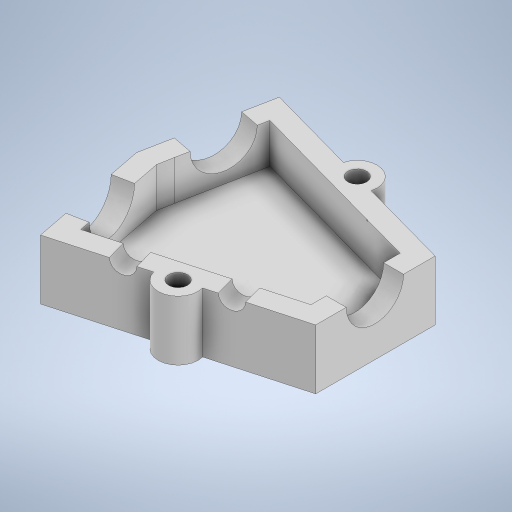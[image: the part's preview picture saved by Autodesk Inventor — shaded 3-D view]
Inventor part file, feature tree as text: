
AUTODESK INVENTOR PART (.ipt)
format: ipt  version: 2024 (Build 280153000, 153)  size: 346,624 bytes
history: native  units: in
note: dims shown in document units (in); Inventor stores cm internally (conversion verified against a paired STEP export)
features: extrude x8, sketch x8, projected_geometry x1
ambient origin geometry x8: Origin, YZ Plane, XZ Plane, XY Plane, X Axis, Y Axis, Z Axis, Center Point
bodies: Solid1 (feature_tree)
feature tree (17):
  extrude  "Extrusion1"  Depth=0.75in
  extrude  "Extrusion3"  Depth=0.75in
  extrude  "Extrusion4"  Depth=0.125in
  extrude  "Extrusion5"  Depth=0.375in TaperAngle=0.0deg
  extrude  "Extrusion6"  Depth=1.0in TaperAngle=0.0deg
  extrude  "Extrusion7"  Depth=1.0in TaperAngle=0.0deg
  extrude  "Extrusion8"  Depth=0.375in TaperAngle=0.0deg
  extrude  "Extrusion9"  Depth=0.375in TaperAngle=0.0deg
  sketch  "Sketch1"  dims[d0=1.0in d1=0.75in]
  sketch  "Sketch3"  dims[d2=0.5in d3=0.75in]
  sketch  "Sketch4"  dims[d4=0.125in d5=0.125in]
  sketch  "Sketch5"  dims[d6=0.125in d7=0.375in d8=0.0in]
  sketch  "Sketch6"  dims[d12=0.36in d13=1.0in d14=0.0in]
  projected_geometry  "Projected Loop1"
  sketch  "Sketch7"  dims[d15=0.36in d16=1.0in d17=0.0in]
  sketch  "Sketch8"  dims[d18=0.36in d19=0.375in d20=0.0in]
  sketch  "Sketch10"  dims[d21=0.125in d22=0.0in d23=0.375in d24=0.0in d25=0.1181in d26=0.1181in d27=0.375in d28=0.0in d29=0.14in d30=0.14in d31=0.15in d32=0.15in d33=0.375in d34=0.0in]
